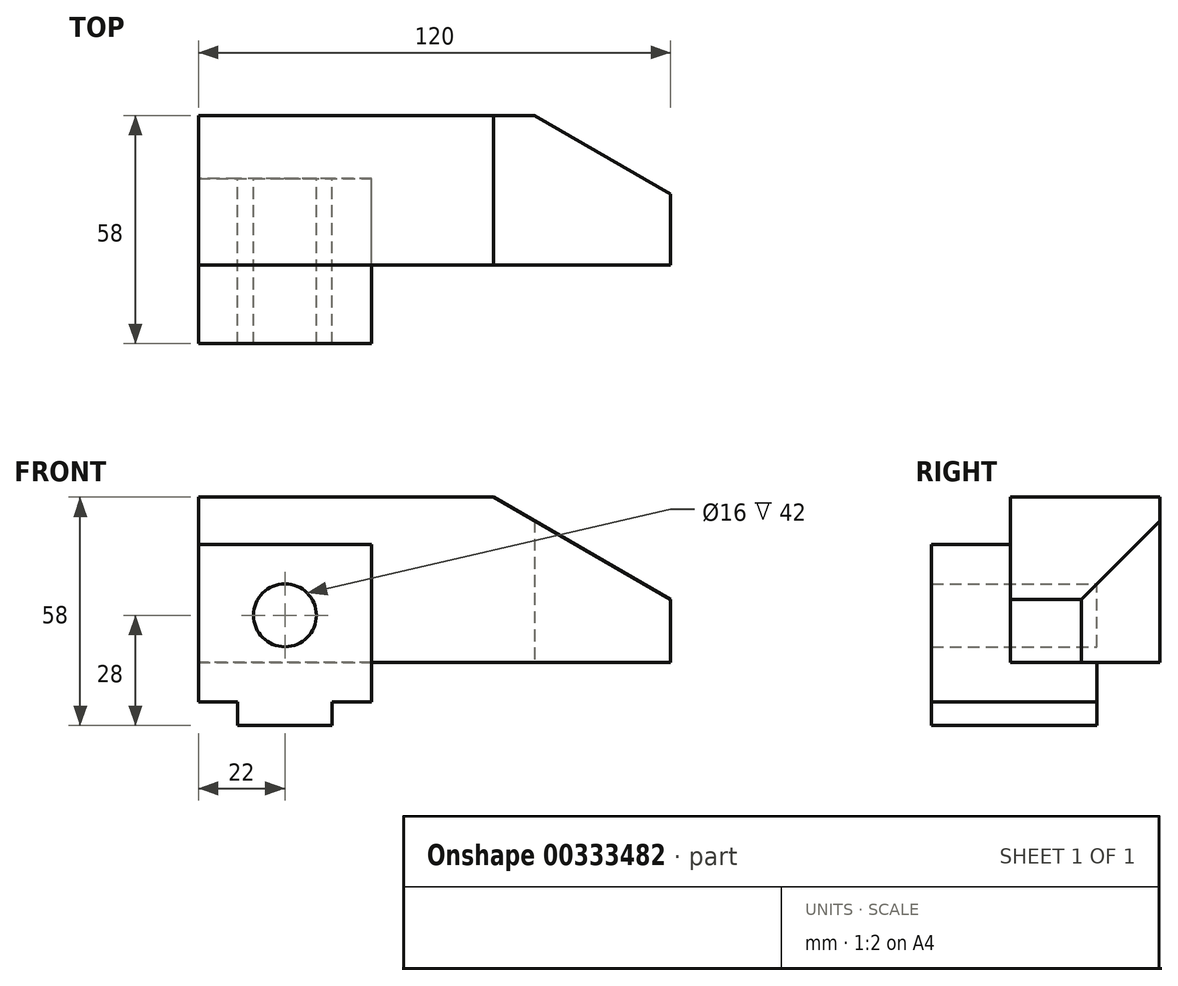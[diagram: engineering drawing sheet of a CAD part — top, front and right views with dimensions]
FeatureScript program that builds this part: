
annotation { "Feature Type Name" : "Feature", "Feature Type Description" : "" }
export const myFeature = defineFeature(function(context is Context, id is Id, definition is map)
    precondition{}
    {
        {
            var Q0;
            Q0=qCreatedBy(makeId("Front.planeOp"),FACE);
            var sketch = newSketch(context, id + "F0", { "sketchPlane" : qUnion([Q0])});
            skLineSegment(sketch, "E0", {"start": v(10, 0) * mm, "end": v(10, 6) * mm});
            skLineSegment(sketch, "E1", {"start": v(10, 6) * mm, "end": v(0, 6) * mm});
            skLineSegment(sketch, "E2", {"start": v(0, 6) * mm, "end": v(0, 46) * mm});
            skLineSegment(sketch, "E3", {"start": v(0, 46) * mm, "end": v(44, 46) * mm});
            skLineSegment(sketch, "E4", {"start": v(44, 46) * mm, "end": v(44, 6) * mm});
            skLineSegment(sketch, "E5", {"start": v(44, 6) * mm, "end": v(34, 6) * mm});
            skLineSegment(sketch, "E6", {"start": v(34, 6) * mm, "end": v(34, 0) * mm});
            skLineSegment(sketch, "E7", {"start": v(34, 0) * mm, "end": v(10, 0) * mm});
            skLineSegment(sketch, "E8", {"start": v(0, 46) * mm, "end": v(0, 58) * mm});
            skLineSegment(sketch, "E9", {"start": v(0, 58) * mm, "end": v(75, 58) * mm});
            skLineSegment(sketch, "E10", {"start": v(75, 58) * mm, "end": v(120, 32.02) * mm});
            skLineSegment(sketch, "E11", {"start": v(120, 32.02) * mm, "end": v(120, 16) * mm});
            skLineSegment(sketch, "E12", {"start": v(120, 16) * mm, "end": v(44, 16) * mm});
            skCircle(sketch, "E13", {"center": v(22, 28) * mm, "radius": 8 * mm});
            skSolve(sketch);
        }
        {
            var Q0;
            Q0=qCreatedBy(makeId("Front.planeOp"),FACE);
            cPlane(context, id + "F1", {"entities" : qUnion([Q0]), "cplaneType" : CPlaneType.OFFSET, "offset" : 16 * mm, "oppositeDirection" : true, "width" : 150 * mm, "height" : 150 * mm});
        }
        {
            var Q0;
            Q0=qCreatedBy(id+"F1.planeOp",FACE);
            var sketch = newSketch(context, id + "F2", { "sketchPlane" : qUnion([Q0])});
            skLineSegment(sketch, "E14", {"start": v(0, 58) * mm, "end": v(75, 58) * mm});
            skLineSegment(sketch, "E15", {"start": v(75, 58) * mm, "end": v(120, 32.02) * mm});
            skLineSegment(sketch, "E16", {"start": v(120, 32.02) * mm, "end": v(120, 16) * mm});
            skLineSegment(sketch, "E17", {"start": v(120, 16) * mm, "end": v(0, 16) * mm});
            skLineSegment(sketch, "E18", {"start": v(0, 16) * mm, "end": v(0, 58) * mm});
            skSolve(sketch);
        }
        {
            var Q0;
            Q0=makeQuery(id+"F0.imprint","IMPRINT",FACE,{"disambiguationData":[TD([[makeQuery(id+"F0.imprint","IMPRINT",EDGE,{"derivedFrom":sQuery(id+"F0.wireOp",EDGE,"E0")}),-1.0]])]});
            extrude(context, id + "F3", {"entities" : qUnion([Q0]), "depth" : 42 * mm});
        }
        {
            var Q0;
            Q0=makeQuery(id+"F2.imprint","IMPRINT",FACE,{"disambiguationData":[TD([[makeQuery(id+"F2.imprint","IMPRINT",EDGE,{"derivedFrom":sQuery(id+"F2.wireOp",EDGE,"E14")}),-1.0]])]});
            extrude(context, id + "F4", {"entities" : qUnion([Q0]), "operationType" : NewBodyOperationType.ADD, "depth" : 38 * mm});
        }
        {
            var Q0;
            Q0=makeQuery(id+"F4.boolean.opBoolean","SPLIT",FACE,{"disambiguationData":[TD([makeQuery(id+"F3.opExtrude","SWEPT_FACE",FACE,{"disambiguationData":[OSD([sQuery(id+"F0.wireOp",EDGE,"E13")])]})])],"derivedFrom":makeQuery(id+"F4.opExtrude","CAP_FACE",FACE,{"disambiguationData":[OSD([sQuery(id+"F2.wireOp",EDGE,"E14"),sQuery(id+"F2.wireOp",EDGE,"E15"),sQuery(id+"F2.wireOp",EDGE,"E16"),sQuery(id+"F2.wireOp",EDGE,"E17"),sQuery(id+"F2.wireOp",EDGE,"E18")])],"isStart":false})});
            extrude(context, id + "F5", {"entities" : qUnion([Q0]), "operationType" : NewBodyOperationType.REMOVE, "oppositeDirection" : true, "depth" : 22 * mm});
        }
        {
            var Q0;
            Q0=makeQuery(id+"F4.opExtrude","SWEPT_FACE",FACE,{"disambiguationData":[OSD([sQuery(id+"F2.wireOp",EDGE,"E17")])]});
            var sketch = newSketch(context, id + "F6", { "sketchPlane" : qUnion([Q0])});
            skLineSegment(sketch, "E19", {"start": v(85.36, -16) * mm, "end": v(120, -16) * mm});
            skLineSegment(sketch, "E20", {"start": v(120, -16) * mm, "end": v(120, 4) * mm});
            skLineSegment(sketch, "E21", {"start": v(120, 4) * mm, "end": v(85.36, -16) * mm});
            skSolve(sketch);
        }
        {
            var Q0;
            Q0=makeQuery(id+"F6.imprint","IMPRINT",FACE,{"disambiguationData":[TD([[makeQuery(id+"F6.imprint","IMPRINT",EDGE,{"derivedFrom":sQuery(id+"F6.wireOp",EDGE,"E19")}),-1.0]])]});
            extrude(context, id + "F7", {"entities" : qUnion([Q0]), "operationType" : NewBodyOperationType.REMOVE, "endBound" : BoundingType.THROUGH_ALL, "oppositeDirection" : true, "depth" : 25 * mm});
        }
    });
